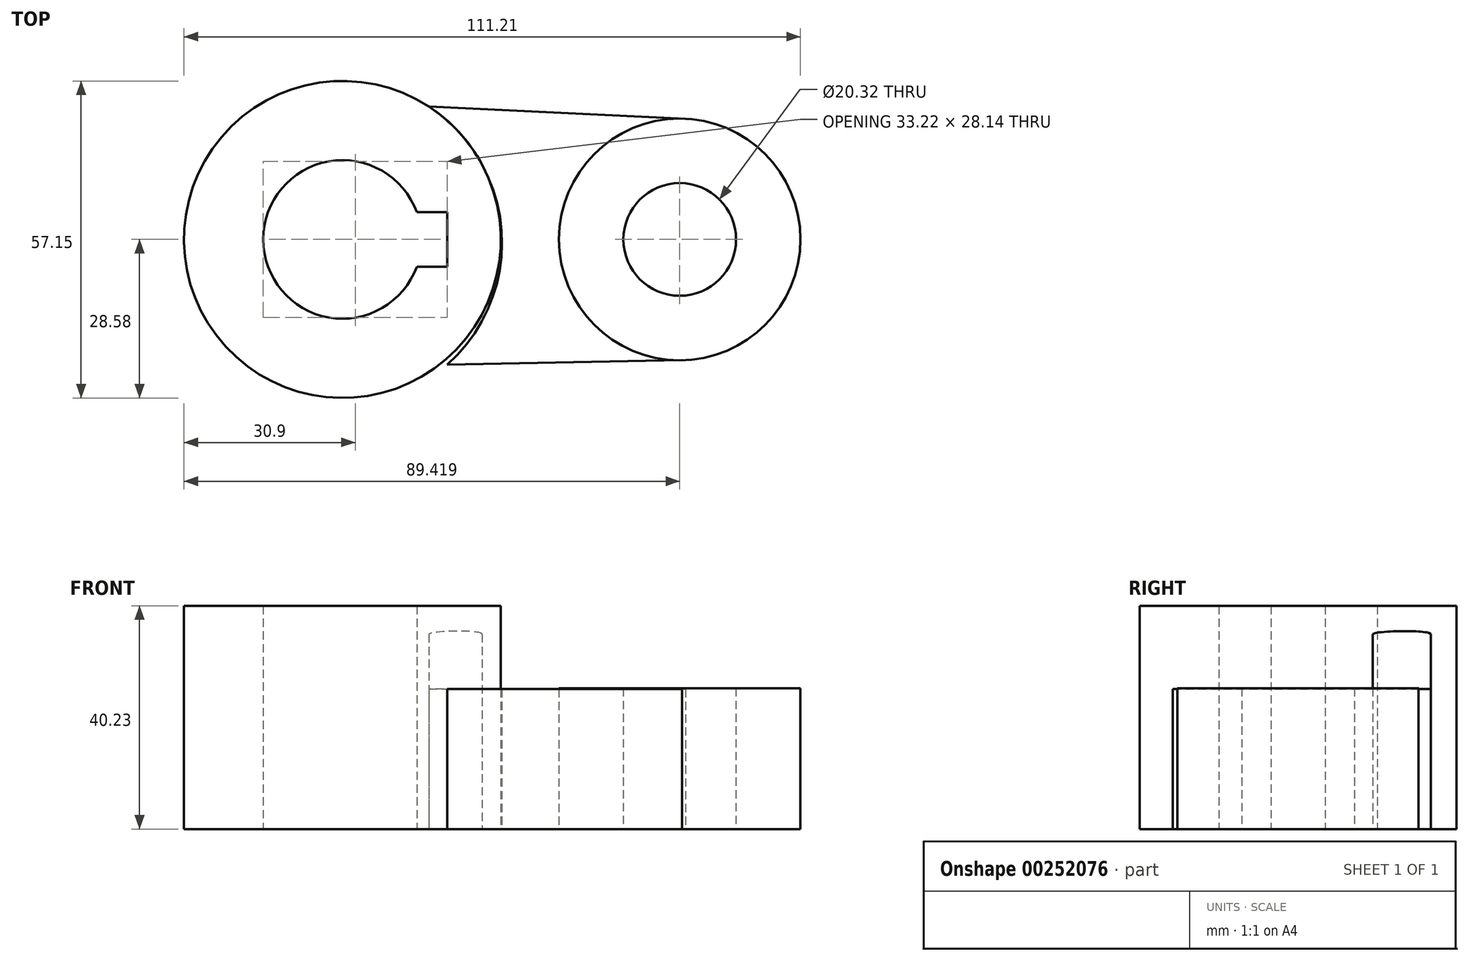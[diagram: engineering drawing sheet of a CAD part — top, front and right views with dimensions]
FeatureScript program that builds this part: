
annotation { "Feature Type Name" : "Feature", "Feature Type Description" : "" }
export const myFeature = defineFeature(function(context is Context, id is Id, definition is map)
    precondition{}
    {
        {
            var Q0;
            Q0=qCreatedBy(makeId("Top.planeOp"),FACE);
            var sketch = newSketch(context, id + "F0", { "sketchPlane" : qUnion([Q0])});
            skCircle(sketch, "E0", {"center": v(-46.96, 0) * mm, "radius": 28.58 * mm});
            skCircle(sketch, "E1", {"center": v(-46.96, 0) * mm, "radius": 14.29 * mm});
            skLineSegment(sketch, "E2.bottom", {"start": v(-28.03, -4.9) * mm, "end": v(-37.32, -4.9) * mm});
            skLineSegment(sketch, "E2.top", {"start": v(-28.03, 4.9) * mm, "end": v(-37.32, 4.9) * mm});
            skLineSegment(sketch, "E2.left", {"start": v(-28.03, -4.9) * mm, "end": v(-28.03, 4.9) * mm});
            skLineSegment(sketch, "E2.right", {"start": v(-37.32, -4.9) * mm, "end": v(-37.32, 4.9) * mm});
            skPoint(sketch, "E2.middle", {"position": v(-32.67, 0) * mm});
            skCircle(sketch, "E3", {"center": v(13.88, 0) * mm, "radius": 10.16 * mm});
            skCircle(sketch, "E4", {"center": v(13.88, 0) * mm, "radius": 21.79 * mm});
            skLineSegment(sketch, "E5", {"start": v(-31.37, 23.95) * mm, "end": v(14.9, 21.76) * mm});
            skLineSegment(sketch, "E6", {"start": v(-28.03, -22.59) * mm, "end": v(14.3, -21.78) * mm});
            skArc(sketch, "E7", {"start": v(14.9, 21.76) * mm, "mid": v(-7.9, 0.3) * mm, "end": v(14.3, -21.78) * mm});
            skArc(sketch, "E8", {"start": v(-28.03, -22.59) * mm, "mid": v(-18.25, 1.5) * mm, "end": v(-31.37, 23.95) * mm});
            skSolve(sketch);
        }
        {
            var Q0;
            Q0=makeQuery(id+"F0.imprint","IMPRINT",FACE,{"disambiguationData":[TD([[makeQuery(id+"F0.imprint","IMPRINT",EDGE,{"derivedFrom":sQuery(id+"F0.wireOp",EDGE,"E0")}),1.0]])]});
            extrude(context, id + "F1", {"entities" : qUnion([Q0]), "depth" : 40.23 * mm});
        }
        {
            var Q0;
            Q0=makeQuery(id+"F1.opExtrude","CAP_EDGE",EDGE,{"disambiguationData":[OSD([sQuery(id+"F0.wireOp",EDGE,"E0")])],"isStart":false});
            fillet(context, id + "F2", {"entities" : qUnion([Q0]), "radius" : 5.08 * mm, "tangentPropagation" : true, "allowEdgeOverflow" : false});
        }
        {
            var Q0;
            Q0=makeQuery(id+"F0.imprint","IMPRINT",FACE,{"disambiguationData":[TD([[makeQuery(id+"F0.imprint","IMPRINT",EDGE,{"derivedFrom":sQuery(id+"F0.wireOp",EDGE,"E3")}),-1.0]])]});
            extrude(context, id + "F3", {"entities" : qUnion([Q0]), "depth" : 25.4 * mm});
        }
        {
            var Q0;
            {var subQ1=sQuery(id+"F0.wireOp",EDGE,"E5");Q0=makeQuery(id+"F0.imprint","IMPRINT",FACE,{"disambiguationData":[TD([[makeQuery(id+"F0.imprint","IMPRINT",EDGE,{"derivedFrom":subQ1}),-1.0]])]});}
            var Q1;
            {var subQ0=sQuery(id+"F0.wireOp",EDGE,"E2.left");Q1=makeQuery(id+"F0.imprint","IMPRINT",FACE,{"disambiguationData":[TD([[makeQuery(id+"F0.imprint","IMPRINT",EDGE,{"derivedFrom":subQ0}),-1.0]])]});}
            extrude(context, id + "F4", {"entities" : qUnion([Q0, Q1]), "depth" : 40.23 * mm});
        }
        {
            var Q0;
            Q0=makeQuery(id+"F4.opExtrude","CAP_FACE",FACE,{"disambiguationData":[OSD([sQuery(id+"F0.wireOp",EDGE,"E0"),sQuery(id+"F0.wireOp",EDGE,"E4"),sQuery(id+"F0.wireOp",EDGE,"E5"),sQuery(id+"F0.wireOp",EDGE,"E6"),sQuery(id+"F0.wireOp",EDGE,"E8")])],"isStart":false});
            extrude(context, id + "F5", {"entities" : qUnion([Q0]), "operationType" : NewBodyOperationType.REMOVE, "oppositeDirection" : true, "depth" : 15 * mm});
        }
    });
